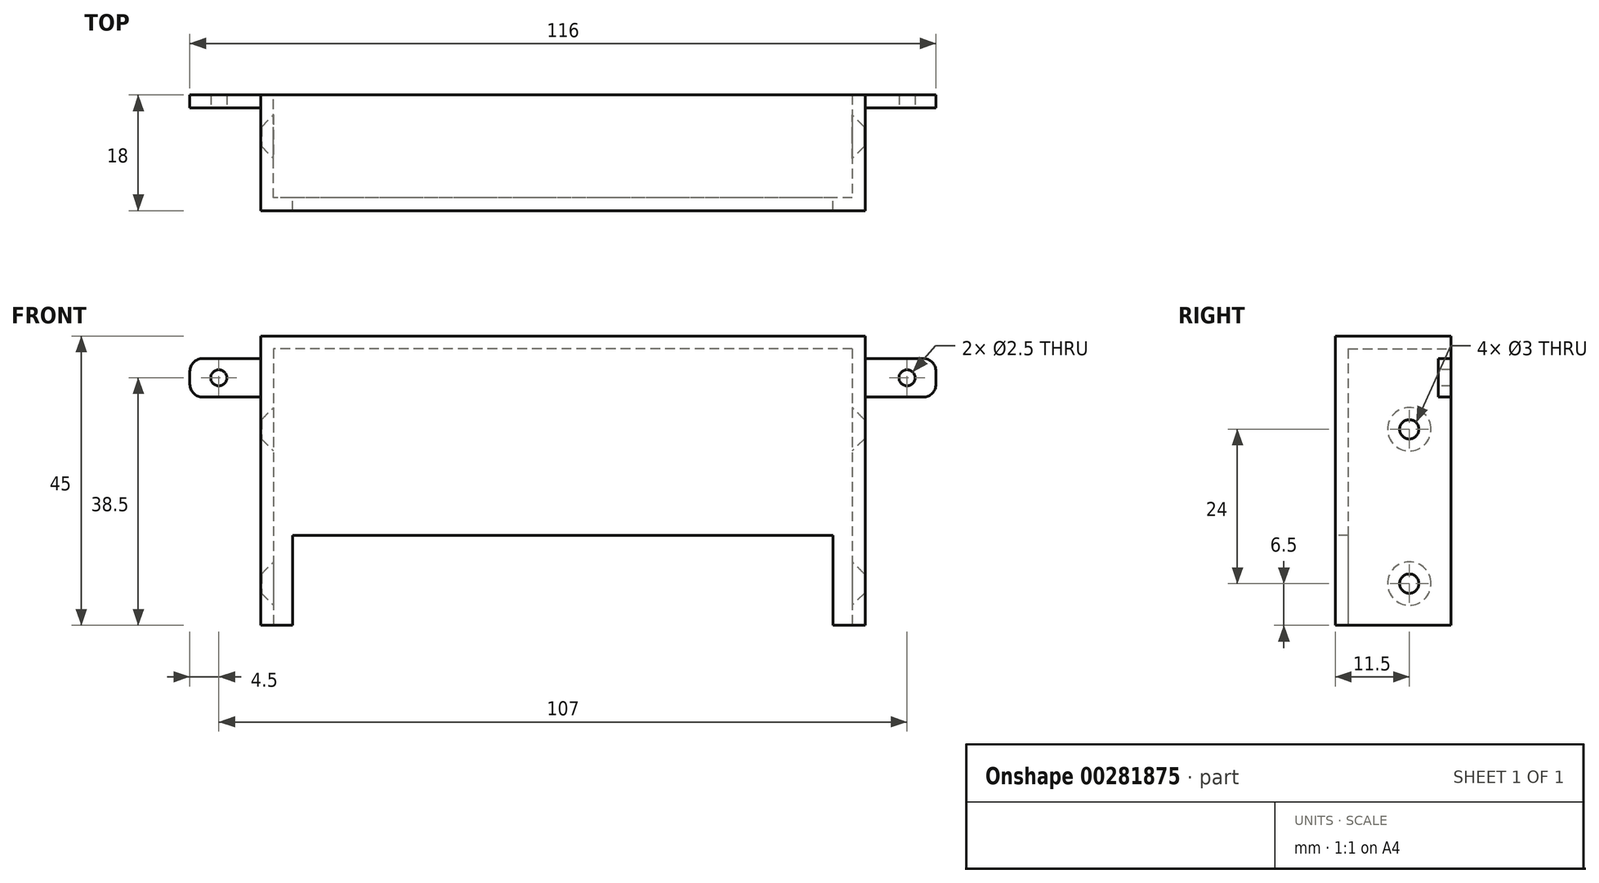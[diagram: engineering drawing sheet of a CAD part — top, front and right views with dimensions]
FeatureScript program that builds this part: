
annotation { "Feature Type Name" : "Feature", "Feature Type Description" : "" }
export const myFeature = defineFeature(function(context is Context, id is Id, definition is map)
    precondition{}
    {
        {
            var Q0;
            Q0=qCreatedBy(makeId("Front.planeOp"),FACE);
            var sketch = newSketch(context, id + "F0", { "sketchPlane" : qUnion([Q0])});
            skLineSegment(sketch, "E0.bottom", {"start": v(47, 22.5) * mm, "end": v(-47, 22.5) * mm});
            skLineSegment(sketch, "E0.top", {"start": v(47, -22.5) * mm, "end": v(-47, -22.5) * mm});
            skLineSegment(sketch, "E0.left", {"start": v(47, 22.5) * mm, "end": v(47, -22.5) * mm});
            skLineSegment(sketch, "E0.right", {"start": v(-47, 22.5) * mm, "end": v(-47, -22.5) * mm});
            skPoint(sketch, "E0.middle", {"position": v(0, 0) * mm});
            skSolve(sketch);
        }
        {
            var Q0;
            Q0=qSketchRegion(id+"F0",true);
            extrude(context, id + "F1", {"entities" : qUnion([Q0]), "depth" : 2 * mm});
        }
        {
            var Q0;
            Q0=makeQuery(id+"F1.opExtrude","CAP_FACE",FACE,{"disambiguationData":[OSD([sQuery(id+"F0.wireOp",EDGE,"E0.bottom"),sQuery(id+"F0.wireOp",EDGE,"E0.top"),sQuery(id+"F0.wireOp",EDGE,"E0.left"),sQuery(id+"F0.wireOp",EDGE,"E0.right")])],"isStart":true});
            var sketch = newSketch(context, id + "F2", { "sketchPlane" : qUnion([Q0])});
            skLineSegment(sketch, "E1.bottom", {"start": v(-47, 22.5) * mm, "end": v(-45, 22.5) * mm});
            skLineSegment(sketch, "E1.top", {"start": v(-47, -22.5) * mm, "end": v(-45, -22.5) * mm});
            skLineSegment(sketch, "E1.left", {"start": v(-47, 22.5) * mm, "end": v(-47, -22.5) * mm});
            skLineSegment(sketch, "E1.right", {"start": v(-45, 22.5) * mm, "end": v(-45, -22.5) * mm});
            skLineSegment(sketch, "E2.bottom", {"start": v(47, 22.5) * mm, "end": v(45, 22.5) * mm});
            skLineSegment(sketch, "E2.top", {"start": v(47, -22.5) * mm, "end": v(45, -22.5) * mm});
            skLineSegment(sketch, "E2.left", {"start": v(47, 22.5) * mm, "end": v(47, -22.5) * mm});
            skLineSegment(sketch, "E2.right", {"start": v(45, 22.5) * mm, "end": v(45, -22.5) * mm});
            skSolve(sketch);
        }
        {
            var Q0;
            Q0=qSketchRegion(id+"F2",true);
            extrude(context, id + "F3", {"entities" : qUnion([Q0]), "operationType" : NewBodyOperationType.ADD, "depth" : 16 * mm});
        }
        {
            var Q0;
            Q0=makeQuery(id+"F3.boolean.opBoolean","MERGE",FACE,{"derivedFrom":[makeQuery(id+"F1.opExtrude","SWEPT_FACE",FACE,{"disambiguationData":[OSD([sQuery(id+"F0.wireOp",EDGE,"E0.bottom")])]}),makeQuery(id+"F3.opExtrude","SWEPT_FACE",FACE,{"disambiguationData":[OSD([sQuery(id+"F2.wireOp",EDGE,"E1.bottom")])]}),makeQuery(id+"F3.opExtrude","SWEPT_FACE",FACE,{"disambiguationData":[OSD([sQuery(id+"F2.wireOp",EDGE,"E2.bottom")])]})]});
            var sketch = newSketch(context, id + "F4", { "sketchPlane" : qUnion([Q0])});
            skLineSegment(sketch, "E3.bottom", {"start": v(-47, -2) * mm, "end": v(47, -2) * mm});
            skLineSegment(sketch, "E3.top", {"start": v(-47, 16) * mm, "end": v(47, 16) * mm});
            skLineSegment(sketch, "E3.left", {"start": v(-47, -2) * mm, "end": v(-47, 16) * mm});
            skLineSegment(sketch, "E3.right", {"start": v(47, -2) * mm, "end": v(47, 16) * mm});
            skSolve(sketch);
        }
        {
            var Q0;
            Q0=qSketchRegion(id+"F4",true);
            extrude(context, id + "F5", {"entities" : qUnion([Q0]), "operationType" : NewBodyOperationType.ADD, "oppositeDirection" : true, "depth" : 2 * mm});
        }
        {
            var Q0;
            Q0=makeQuery(id+"F3.boolean.opBoolean","MERGE",FACE,{"derivedFrom":[makeQuery(id+"F1.opExtrude","SWEPT_FACE",FACE,{"disambiguationData":[OSD([sQuery(id+"F0.wireOp",EDGE,"E0.left")])]}),makeQuery(id+"F3.opExtrude","SWEPT_FACE",FACE,{"disambiguationData":[OSD([sQuery(id+"F2.wireOp",EDGE,"E1.left")])]})]});
            var sketch = newSketch(context, id + "F6", { "sketchPlane" : qUnion([Q0])});
            skLineSegment(sketch, "E4", {"start": v(16, 22.5) * mm, "end": v(16, -22.5) * mm, "construction": true});
            skLineSegment(sketch, "E5", {"start": v(16, -22.5) * mm, "end": v(-2, -22.5) * mm, "construction": true});
            skLineSegment(sketch, "E6", {"start": v(-2, -22.5) * mm, "end": v(-2, 0) * mm, "construction": true});
            skLineSegment(sketch, "E7", {"start": v(-2, 0) * mm, "end": v(44.18, 0) * mm, "construction": true});
            skLineSegment(sketch, "E8.bottom", {"start": v(16, 19) * mm, "end": v(14, 19) * mm});
            skLineSegment(sketch, "E8.top", {"start": v(16, 13) * mm, "end": v(14, 13) * mm});
            skLineSegment(sketch, "E8.left", {"start": v(16, 19) * mm, "end": v(16, 13) * mm});
            skLineSegment(sketch, "E8.right", {"start": v(14, 19) * mm, "end": v(14, 13) * mm});
            skLineSegment(sketch, "E9.bottom", {"start": v(16, -13) * mm, "end": v(14, -13) * mm});
            skLineSegment(sketch, "E9.top", {"start": v(16, -19) * mm, "end": v(14, -19) * mm});
            skLineSegment(sketch, "E9.left", {"start": v(16, -13) * mm, "end": v(16, -19) * mm});
            skLineSegment(sketch, "E9.right", {"start": v(14, -13) * mm, "end": v(14, -19) * mm});
            skSolve(sketch);
        }
        {
            var Q0;
            Q0=qSketchRegion(id+"F6",true);
            extrude(context, id + "F7", {"entities" : qUnion([Q0]), "operationType" : NewBodyOperationType.ADD, "depth" : 11 * mm});
        }
        {
            var Q0;
            Q0=makeQuery(id+"F7.opExtrude","SWEPT_FACE",FACE,{"disambiguationData":[OSD([sQuery(id+"F6.wireOp",EDGE,"E8.right")])]});
            var sketch = newSketch(context, id + "F8", { "sketchPlane" : qUnion([Q0])});
            skCircle(sketch, "E10", {"center": v(53.5, 16) * mm, "radius": 1.25 * mm});
            skCircle(sketch, "E11", {"center": v(53.5, -16) * mm, "radius": 1.5 * mm});
            skSolve(sketch);
        }
        {
            var Q0;
            Q0=qSketchRegion(id+"F8",true);
            extrude(context, id + "F9", {"entities" : qUnion([Q0]), "operationType" : NewBodyOperationType.REMOVE, "oppositeDirection" : true, "depth" : 25 * mm});
        }
        {
            var Q0;
            Q0=makeQuery(id+"F7.opExtrude","CAP_EDGE",EDGE,{"disambiguationData":[OSD([sQuery(id+"F6.wireOp",EDGE,"E9.top")])],"isStart":false});
            var Q1;
            Q1=makeQuery(id+"F7.opExtrude","CAP_EDGE",EDGE,{"disambiguationData":[OSD([sQuery(id+"F6.wireOp",EDGE,"E9.bottom")])],"isStart":false});
            var Q2;
            Q2=makeQuery(id+"F7.opExtrude","CAP_EDGE",EDGE,{"disambiguationData":[OSD([sQuery(id+"F6.wireOp",EDGE,"E8.bottom")])],"isStart":false});
            var Q3;
            Q3=makeQuery(id+"F7.opExtrude","CAP_EDGE",EDGE,{"disambiguationData":[OSD([sQuery(id+"F6.wireOp",EDGE,"E8.top")])],"isStart":false});
            var Q4;
            Q4=makeQuery(id+"F7.opExtrude","CAP_EDGE",EDGE,{"disambiguationData":[OSD([sQuery(id+"F6.wireOp",EDGE,"E9.right")])],"isStart":true});
            var Q5;
            Q5=makeQuery(id+"F7.opExtrude","CAP_EDGE",EDGE,{"disambiguationData":[OSD([sQuery(id+"F6.wireOp",EDGE,"E8.right")])],"isStart":true});
            fillet(context, id + "F10", {"entities" : qUnion([Q0, Q1, Q2, Q3, Q4, Q5]), "radius" : 2 * mm, "tangentPropagation" : true, "allowEdgeOverflow" : false});
        }
        {
            var Q0;
            Q0=makeQuery(id+"F1.opExtrude","SWEPT_BODY",BODY,{"disambiguationData":[OSD([sQuery(id+"F0.wireOp",EDGE,"E0.bottom"),sQuery(id+"F0.wireOp",EDGE,"E0.top"),sQuery(id+"F0.wireOp",EDGE,"E0.left"),sQuery(id+"F0.wireOp",EDGE,"E0.right")])]});
            var Q1;
            Q1=qCreatedBy(makeId("Right.planeOp"),FACE);
            mirror(context, id + "F11", {"operationType" : NewBodyOperationType.ADD, "entities" : qUnion([Q0]), "mirrorPlane" : qUnion([Q1])});
        }
        {
            var Q0;
            Q0=makeQuery(id+"F1.opExtrude","CAP_FACE",FACE,{"disambiguationData":[OSD([sQuery(id+"F0.wireOp",EDGE,"E0.bottom"),sQuery(id+"F0.wireOp",EDGE,"E0.top"),sQuery(id+"F0.wireOp",EDGE,"E0.left"),sQuery(id+"F0.wireOp",EDGE,"E0.right")])],"isStart":false});
            var sketch = newSketch(context, id + "F12", { "sketchPlane" : qUnion([Q0])});
            skLineSegment(sketch, "E12.bottom", {"start": v(47, -22.5) * mm, "end": v(66.27, -22.5) * mm});
            skLineSegment(sketch, "E12.top", {"start": v(47, -7.64) * mm, "end": v(66.27, -7.64) * mm});
            skLineSegment(sketch, "E12.left", {"start": v(47, -22.5) * mm, "end": v(47, -7.64) * mm});
            skLineSegment(sketch, "E12.right", {"start": v(66.27, -22.5) * mm, "end": v(66.27, -7.64) * mm});
            skLineSegment(sketch, "E13.bottom", {"start": v(-47, -22.5) * mm, "end": v(-63.88, -22.5) * mm});
            skLineSegment(sketch, "E13.top", {"start": v(-47, -7.22) * mm, "end": v(-63.88, -7.22) * mm});
            skLineSegment(sketch, "E13.left", {"start": v(-47, -22.5) * mm, "end": v(-47, -7.22) * mm});
            skLineSegment(sketch, "E13.right", {"start": v(-63.88, -22.5) * mm, "end": v(-63.88, -7.22) * mm});
            skSolve(sketch);
        }
        {
            var Q0;
            Q0=qSketchRegion(id+"F12",true);
            extrude(context, id + "F13", {"entities" : qUnion([Q0]), "operationType" : NewBodyOperationType.REMOVE, "oppositeDirection" : true, "depth" : 25 * mm});
        }
        {
            var Q0;
            Q0=makeQuery(id+"F13.boolean.opBoolean","MERGE",FACE,{"derivedFrom":[makeQuery(id+"F3.boolean.opBoolean","MERGE",FACE,{"derivedFrom":[makeQuery(id+"F1.opExtrude","SWEPT_FACE",FACE,{"disambiguationData":[OSD([sQuery(id+"F0.wireOp",EDGE,"E0.right")])]}),makeQuery(id+"F3.opExtrude","SWEPT_FACE",FACE,{"disambiguationData":[OSD([sQuery(id+"F2.wireOp",EDGE,"E2.left")])]})]}),makeQuery(id+"F13.opExtrude","SWEPT_FACE",FACE,{"disambiguationData":[OSD([sQuery(id+"F12.wireOp",EDGE,"E13.left")])]})]});
            var sketch = newSketch(context, id + "F14", { "sketchPlane" : qUnion([Q0])});
            skCircle(sketch, "E14", {"center": v(-9.5, -16) * mm, "radius": 1.5 * mm});
            skSolve(sketch);
        }
        {
            var Q0;
            Q0=qSketchRegion(id+"F14",true);
            extrude(context, id + "F15", {"entities" : qUnion([Q0]), "operationType" : NewBodyOperationType.REMOVE, "oppositeDirection" : true, "depth" : 100 * mm});
        }
        {
            var Q0;
            Q0=makeQuery(id+"F13.boolean.opBoolean","MERGE",FACE,{"derivedFrom":[makeQuery(id+"F3.boolean.opBoolean","MERGE",FACE,{"derivedFrom":[makeQuery(id+"F1.opExtrude","SWEPT_FACE",FACE,{"disambiguationData":[OSD([sQuery(id+"F0.wireOp",EDGE,"E0.right")])]}),makeQuery(id+"F3.opExtrude","SWEPT_FACE",FACE,{"disambiguationData":[OSD([sQuery(id+"F2.wireOp",EDGE,"E2.left")])]})]}),makeQuery(id+"F13.opExtrude","SWEPT_FACE",FACE,{"disambiguationData":[OSD([sQuery(id+"F12.wireOp",EDGE,"E13.left")])]})]});
            var sketch = newSketch(context, id + "F16", { "sketchPlane" : qUnion([Q0])});
            skCircle(sketch, "E15", {"center": v(-9.5, 8) * mm, "radius": 1.5 * mm});
            skSolve(sketch);
        }
        {
            var Q0;
            Q0=qSketchRegion(id+"F16",true);
            extrude(context, id + "F17", {"entities" : qUnion([Q0]), "operationType" : NewBodyOperationType.REMOVE, "oppositeDirection" : true, "depth" : 100 * mm});
        }
        {
            var Q0;
            Q0=makeQuery(id+"F17.boolean.opBoolean","INTERSECT",EDGE,{"derivedFrom":[makeQuery(id+"F3.opExtrude","SWEPT_FACE",FACE,{"disambiguationData":[OSD([sQuery(id+"F2.wireOp",EDGE,"E1.right")])]}),makeQuery(id+"F17.opExtrude","SWEPT_FACE",FACE,{"disambiguationData":[OSD([sQuery(id+"F16.wireOp",EDGE,"E15")])]})]});
            var Q1;
            Q1=makeQuery(id+"F15.boolean.opBoolean","INTERSECT",EDGE,{"derivedFrom":[makeQuery(id+"F3.opExtrude","SWEPT_FACE",FACE,{"disambiguationData":[OSD([sQuery(id+"F2.wireOp",EDGE,"E1.right")])]}),makeQuery(id+"F15.opExtrude","SWEPT_FACE",FACE,{"disambiguationData":[OSD([sQuery(id+"F14.wireOp",EDGE,"E14")])]})]});
            var Q2;
            Q2=makeQuery(id+"F17.boolean.opBoolean","INTERSECT",EDGE,{"derivedFrom":[makeQuery(id+"F3.opExtrude","SWEPT_FACE",FACE,{"disambiguationData":[OSD([sQuery(id+"F2.wireOp",EDGE,"E2.right")])]}),makeQuery(id+"F17.opExtrude","SWEPT_FACE",FACE,{"disambiguationData":[OSD([sQuery(id+"F16.wireOp",EDGE,"E15")])]})]});
            var Q3;
            Q3=makeQuery(id+"F15.boolean.opBoolean","INTERSECT",EDGE,{"derivedFrom":[makeQuery(id+"F3.opExtrude","SWEPT_FACE",FACE,{"disambiguationData":[OSD([sQuery(id+"F2.wireOp",EDGE,"E2.right")])]}),makeQuery(id+"F15.opExtrude","SWEPT_FACE",FACE,{"disambiguationData":[OSD([sQuery(id+"F14.wireOp",EDGE,"E14")])]})]});
            chamfer(context, id + "F18", {"entities" : qUnion([Q0, Q1, Q2, Q3]), "width" : 1.87 * mm, "tangentPropagation" : true});
        }
        {
            var Q0;
            Q0=makeQuery(id+"F1.opExtrude","CAP_FACE",FACE,{"disambiguationData":[OSD([sQuery(id+"F0.wireOp",EDGE,"E0.bottom"),sQuery(id+"F0.wireOp",EDGE,"E0.top"),sQuery(id+"F0.wireOp",EDGE,"E0.left"),sQuery(id+"F0.wireOp",EDGE,"E0.right")])],"isStart":false});
            var sketch = newSketch(context, id + "F19", { "sketchPlane" : qUnion([Q0])});
            skLineSegment(sketch, "E16.bottom", {"start": v(42, -8.5) * mm, "end": v(-42, -8.5) * mm});
            skLineSegment(sketch, "E16.top", {"start": v(42, -36.5) * mm, "end": v(-42, -36.5) * mm});
            skLineSegment(sketch, "E16.left", {"start": v(42, -8.5) * mm, "end": v(42, -36.5) * mm});
            skLineSegment(sketch, "E16.right", {"start": v(-42, -8.5) * mm, "end": v(-42, -36.5) * mm});
            skPoint(sketch, "E16.middle", {"position": v(0, -22.5) * mm});
            skSolve(sketch);
        }
        {
            var Q0;
            Q0=qSketchRegion(id+"F19",true);
            extrude(context, id + "F20", {"entities" : qUnion([Q0]), "operationType" : NewBodyOperationType.REMOVE, "oppositeDirection" : true, "depth" : 25 * mm});
        }
    });
